# Revit family: Hager-Volta-IP30-Surface_mounted-vuoto-CH-it
name_source: partatom
category: Electrical Equipment
units: mm (PartAtom-declared; Revit-internal decimal feet)

## family parameters
Cut with Voids When Loaded = No
Host = Face
Panel Configuration = Two Columns, Circuits Across
Part Type = Panelboard
Room Calculation Point = No
Round Connector Dimension = Use Diameter
Shared = No

## types (1)
- A parete IP30 L305 A640 P96.5 12 Unità di divisione - VA48MD
    Default Elevation = 0 mm  [stored 0 ft]
    EF000003 - Tipo di montaggio = EV000384 - A parete
    EF000008 - Larghezza = 305 mm  [stored 1.00066 ft]
    EF000040 - Altezza = 640 mm  [stored 2.09974 ft]
    EF000049 - profondità = 96 mm  [stored 0.314961 ft]
    EF000116 - numero RAL = 9010
    EF000118 - con piastra di montaggio = Yes
    EF000218 - profondità di incasso = 0 mm  [stored 0 ft]
    EF000266 - numero di file = 0
    EF000332 - Altezza della parte incassata = 0 mm  [stored 0 ft]
    EF000339 - tipo di copertura = EV000494 - senza
    EF000846 - larghezza di montaggio = 0 mm  [stored 0 ft]
    EF001062 - esecuzione EMC = No
    EF001088 - possibilità di applicazione = Yes
    EF001131 - profondità interna = 0 mm  [stored 0 ft]
    EF001134 - barra DIN = No
    EF002950 - Numero moduli DIN = 12
    EF005474 - grado di protezione (IP) = EV006410 - IP30
    EF006244 - coperchio/porta trasparente = No
    EF006306 - con serratura = No
    EF009212 - esecuzione coperchio = EV009916 - con taglio
    EF015776 - Morsettiera di terra = No
    EF015777 - Morsettiera neutra = No
    EF015941 - Segnale di passaggio porta = No
    HG000001 - Numero di colonne = 0
    HG000002 - Con porta = No
    HG000003 - Gamma = Volta
    HG000004 - Codice produttore = VA48MD
    HG000005 - Spessore = 3 mm  [stored 0.00984252 ft]
    HG000006 - Ad incasso = No
    HG000007 - Numero di colonne vuote = 0
    HG000008 - Numero di file vuote = 0
    HG000009 - Porta doppia a battente = No
    HG000010 - Porte asimmetriche = No
    HG000011 - File vuote nella parte basse = No
    HG000017 - Distanza tra i poli = 18 mm  [stored 0.0590551 ft]
    Manufacturer = Hager
    Model = VA48MD
    Type Comments = Volta

note: [stored X ft] marks values corroborated as IEEE doubles in the binary element streams (Revit-internal decimal feet)

## geometry (parser evidence)
native form markers: Sweep x16
no freeform markers — native parametric forms only
